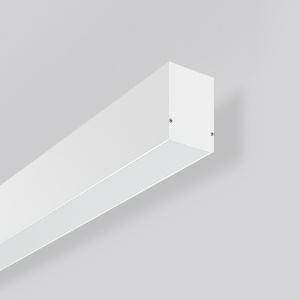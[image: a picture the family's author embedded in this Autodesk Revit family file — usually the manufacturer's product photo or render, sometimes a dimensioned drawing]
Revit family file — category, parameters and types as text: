
# Revit family: less_is_more_50_312612_002_1_76_20e5
name_source: partatom
category: Lighting Fixtures
units: mm (PartAtom-declared; Revit-internal decimal feet)

## family parameters
Cut with Voids When Loaded = No
Host = Face
Light Source = No
Part Type = Normal
Room Calculation Point = No
Round Connector Dimension = Use Diameter
Shared = No

## types (1)
- LESS IS MORE 50 (1 x LED Modul 840, 4100 lm, 4000)
    Apparent Load = 30 VA
    CIE Flux Codes = 48 80 96 50 100
    Color Rendering = 80
    Color Temperature = 4000
    Default Elevation = 1800 mm
    Description = Series: LESS IS MORE 50
Linear wall luminaires. Housing: extruded aluminium profile, powder-coated. End cap aluminium powder-coated. Diffuser made of non-yellowing plastic (PMMA), opal. Direct 50%, indirect 50% light emission. Suitable for Wall (surface). LED unit with integrated converter interchangeable and removable. Suitable for through-wiring. With sensors or as a safety luminaire on request. 
Colour: traffic white, matt (RAL 9016)
Length: 1687 mm
Width: 67 mm
Height: 75 mm
Lamp: LED
Socket: without socket
Colour temperature: 4000K
Colour rendering index (CRI): 80
Light source: LED
Socket lamp2: Without base
Colour temperature: 4000K
Colour rendering index (CRI) 2: 80
System power: 30 W
Rated luminous flux: 4100 lm
Luminous efficiency: 137 lm/W
Control gear: Converter, dimmable, DALI
Control gear: Converter, dimmable, DALI
Protection class: I
Type of protection: IP 20
    Height = 75 mm
    Lamp = 1 x LED Modul 840
    Lamp Light Flux = 4100 lm
    Lamp count = 1
    Length = 1687 mm
    Lifetime = 50000 h
    Luminous efficacy = 137 lm/W
    Manufacturer = RZB
    ModVariant = No
    Model = 312612.002.1.76
    Mounting Place = Wall
    Mounting Type = Surface mounted
    Number of Poles = 1
    OnlyDefault = Yes
    Power Factor = 1
    Product Name = LESS IS MORE 50
    Product group = Surface mounted LED linear luminaires
    ProductGroupID = 2007
    Protection Class = Protection class I
    Protection Degree = IP 20
    RLX_Detail_Level = 1
    RLX_Emergency_Light_Flux = 0 lm
    RLX_Emergency_Type = 0
    RLX_Emergency_Type_DB = No
    RlxData = <blob elided: 39621 chars, md5=9bb3456f>
    Socket = socket
    Standby Power = 0 W
    System Light Flux = 4100 lm
    System Power = 30 W
    Type Comments = Product without accessories
    Type Image = 312606.002.jpg
    URL = http://relux.com
    VarID = ---
    Voltage = 0 V
    Weight = 0.00 kg
    Width = 67 mm

## geometry (parser evidence)
native form markers: Blend x4, Sweep x13
no freeform markers — native parametric forms only
